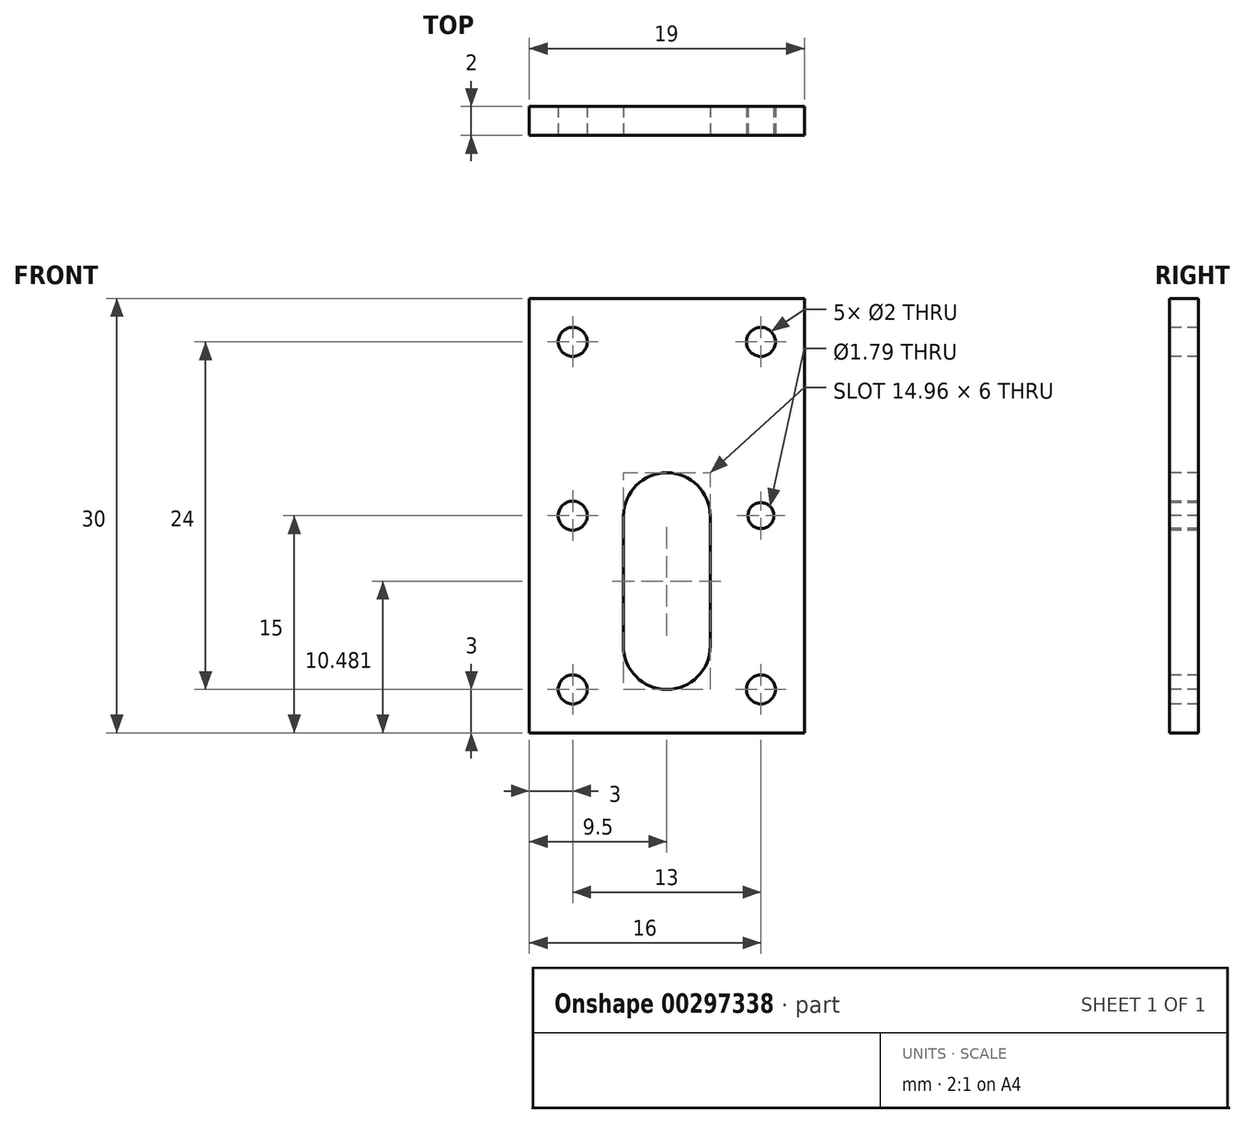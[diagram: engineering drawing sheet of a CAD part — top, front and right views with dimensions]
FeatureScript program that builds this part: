
annotation { "Feature Type Name" : "Feature", "Feature Type Description" : "" }
export const myFeature = defineFeature(function(context is Context, id is Id, definition is map)
    precondition{}
    {
        {
            var Q0;
            Q0=qCreatedBy(makeId("Front.planeOp"),FACE);
            var sketch = newSketch(context, id + "F0", { "sketchPlane" : qUnion([Q0])});
            skLineSegment(sketch, "E0.bottom", {"start": v(9.5, 15) * mm, "end": v(-9.5, 15) * mm});
            skLineSegment(sketch, "E0.top", {"start": v(9.5, -15) * mm, "end": v(-9.5, -15) * mm});
            skLineSegment(sketch, "E0.left", {"start": v(9.5, 15) * mm, "end": v(9.5, -15) * mm});
            skLineSegment(sketch, "E0.right", {"start": v(-9.5, 15) * mm, "end": v(-9.5, -15) * mm});
            skPoint(sketch, "E0.middle", {"position": v(0, 0) * mm});
            skSolve(sketch);
        }
        {
            var Q0;
            Q0 = qSketchRegion(id + "F0", true);
            extrude(context, id + "F1", {"entities" : qUnion([Q0]), "depth" : 5 * mm});
        }
        {
            var Q0;
            Q0=makeQuery(id+"F1.opExtrude","CAP_FACE",FACE,{"disambiguationData":[OSD([sQuery(id+"F0.wireOp",EDGE,"E0.bottom"),sQuery(id+"F0.wireOp",EDGE,"E0.top"),sQuery(id+"F0.wireOp",EDGE,"E0.left"),sQuery(id+"F0.wireOp",EDGE,"E0.right")])],"isStart":false});
            var sketch = newSketch(context, id + "F2", { "sketchPlane" : qUnion([Q0])});
            skArc(sketch, "E1", {"start": v(-3, -9) * mm, "mid": v(0, -12) * mm, "end": v(3, -9) * mm});
            skArc(sketch, "E2", {"start": v(3, 0) * mm, "mid": v(0, 2.96) * mm, "end": v(-3, 0) * mm});
            skLineSegment(sketch, "E3", {"start": v(-3, 0) * mm, "end": v(-3, -9) * mm});
            skLineSegment(sketch, "E4", {"start": v(3, 0) * mm, "end": v(3, -9) * mm});
            skSolve(sketch);
        }
        {
            var Q0;
            Q0 = qSketchRegion(id + "F2", true);
            extrude(context, id + "F3", {"entities" : qUnion([Q0]), "operationType" : NewBodyOperationType.REMOVE, "oppositeDirection" : true, "depth" : 3 * mm});
        }
        {
            var Q0;
            Q0=makeQuery(id+"F3.boolean.opBoolean","COPY",FACE,{"derivedFrom":makeQuery(id+"F3.opExtrude","CAP_FACE",FACE,{"disambiguationData":[OSD([sQuery(id+"F2.wireOp",EDGE,"eL8tKZWk-Lk8S-ufO3-2oGP-yhKa9hkrRPHb.bottom"),sQuery(id+"F2.wireOp",EDGE,"eL8tKZWk-Lk8S-ufO3-2oGP-yhKa9hkrRPHb.left"),sQuery(id+"F2.wireOp",EDGE,"eL8tKZWk-Lk8S-ufO3-2oGP-yhKa9hkrRPHb.right"),sQuery(id+"F2.wireOp",EDGE,"E1")])],"isStart":false})});
            var sketch = newSketch(context, id + "F4", { "sketchPlane" : qUnion([Q0])});
            skLineSegment(sketch, "E5.bottom", {"start": v(-6.5, 12) * mm, "end": v(6.5, 12) * mm, "construction": true});
            skLineSegment(sketch, "E5.top", {"start": v(-6.5, -12) * mm, "end": v(6.5, -12) * mm, "construction": true});
            skLineSegment(sketch, "E5.left", {"start": v(-6.5, 12) * mm, "end": v(-6.5, -12) * mm, "construction": true});
            skLineSegment(sketch, "E5.right", {"start": v(6.5, 12) * mm, "end": v(6.5, -12) * mm, "construction": true});
            skCircle(sketch, "E6", {"center": v(-6.5, 12) * mm, "radius": 1 * mm});
            skCircle(sketch, "E7", {"center": v(6.5, 12) * mm, "radius": 1 * mm});
            skCircle(sketch, "E8", {"center": v(6.5, -12) * mm, "radius": 1 * mm});
            skCircle(sketch, "E9", {"center": v(-6.5, -12) * mm, "radius": 1 * mm});
            skCircle(sketch, "E10", {"center": v(-6.5, 0) * mm, "radius": 1 * mm});
            skCircle(sketch, "E11", {"center": v(6.5, 0) * mm, "radius": 0.9 * mm});
            skSolve(sketch);
        }
        {
            var Q0;
            Q0 = qSketchRegion(id + "F4", true);
            extrude(context, id + "F5", {"entities" : qUnion([Q0]), "operationType" : NewBodyOperationType.REMOVE, "oppositeDirection" : true, "depth" : 25 * mm});
        }
        {
            var Q0;
            Q0 = qSketchRegion(id + "F4", true);
            extrude(context, id + "F6", {"entities" : qUnion([Q0]), "operationType" : NewBodyOperationType.REMOVE, "depth" : 25 * mm});
        }
        {
            var Q0;
            Q0=makeQuery(id+"F1.opExtrude","CAP_FACE",FACE,{"disambiguationData":[OSD([sQuery(id+"F0.wireOp",EDGE,"E0.bottom"),sQuery(id+"F0.wireOp",EDGE,"E0.top"),sQuery(id+"F0.wireOp",EDGE,"E0.left"),sQuery(id+"F0.wireOp",EDGE,"E0.right")])],"isStart":false});
            var sketch = newSketch(context, id + "F7", { "sketchPlane" : qUnion([Q0])});
            skLineSegment(sketch, "E12.bottom", {"start": v(-20.88, 22.1) * mm, "end": v(22.71, 22.1) * mm});
            skLineSegment(sketch, "E12.top", {"start": v(-20.88, -26.48) * mm, "end": v(22.71, -26.48) * mm});
            skLineSegment(sketch, "E12.left", {"start": v(-20.88, 22.1) * mm, "end": v(-20.88, -26.48) * mm});
            skLineSegment(sketch, "E12.right", {"start": v(22.71, 22.1) * mm, "end": v(22.71, -26.48) * mm});
            skSolve(sketch);
        }
        {
            var Q0;
            Q0 = qSketchRegion(id + "F7", true);
            extrude(context, id + "F8", {"entities" : qUnion([Q0]), "operationType" : NewBodyOperationType.REMOVE, "oppositeDirection" : true, "depth" : 2 * mm});
        }
        {
            var Q0;
            Q0=makeQuery(id+"F1.opExtrude","CAP_FACE",FACE,{"disambiguationData":[OSD([sQuery(id+"F0.wireOp",EDGE,"E0.bottom"),sQuery(id+"F0.wireOp",EDGE,"E0.top"),sQuery(id+"F0.wireOp",EDGE,"E0.left"),sQuery(id+"F0.wireOp",EDGE,"E0.right")])],"isStart":true});
            var sketch = newSketch(context, id + "F9", { "sketchPlane" : qUnion([Q0])});
            skLineSegment(sketch, "E13.bottom", {"start": v(-26.38, 29.62) * mm, "end": v(26.52, 29.62) * mm});
            skLineSegment(sketch, "E13.top", {"start": v(-26.38, -31.37) * mm, "end": v(26.52, -31.37) * mm});
            skLineSegment(sketch, "E13.left", {"start": v(-26.38, 29.62) * mm, "end": v(-26.38, -31.37) * mm});
            skLineSegment(sketch, "E13.right", {"start": v(26.52, 29.62) * mm, "end": v(26.52, -31.37) * mm});
            skSolve(sketch);
        }
        {
            var Q0;
            Q0 = qSketchRegion(id + "F9", true);
            extrude(context, id + "F10", {"entities" : qUnion([Q0]), "operationType" : NewBodyOperationType.REMOVE, "oppositeDirection" : true, "depth" : 1 * mm});
        }
        {
            var Q0;
            Q0 = qSketchRegion(id + "F2", true);
            extrude(context, id + "F11", {"entities" : qUnion([Q0]), "operationType" : NewBodyOperationType.REMOVE, "oppositeDirection" : true, "depth" : 25 * mm});
        }
    });
